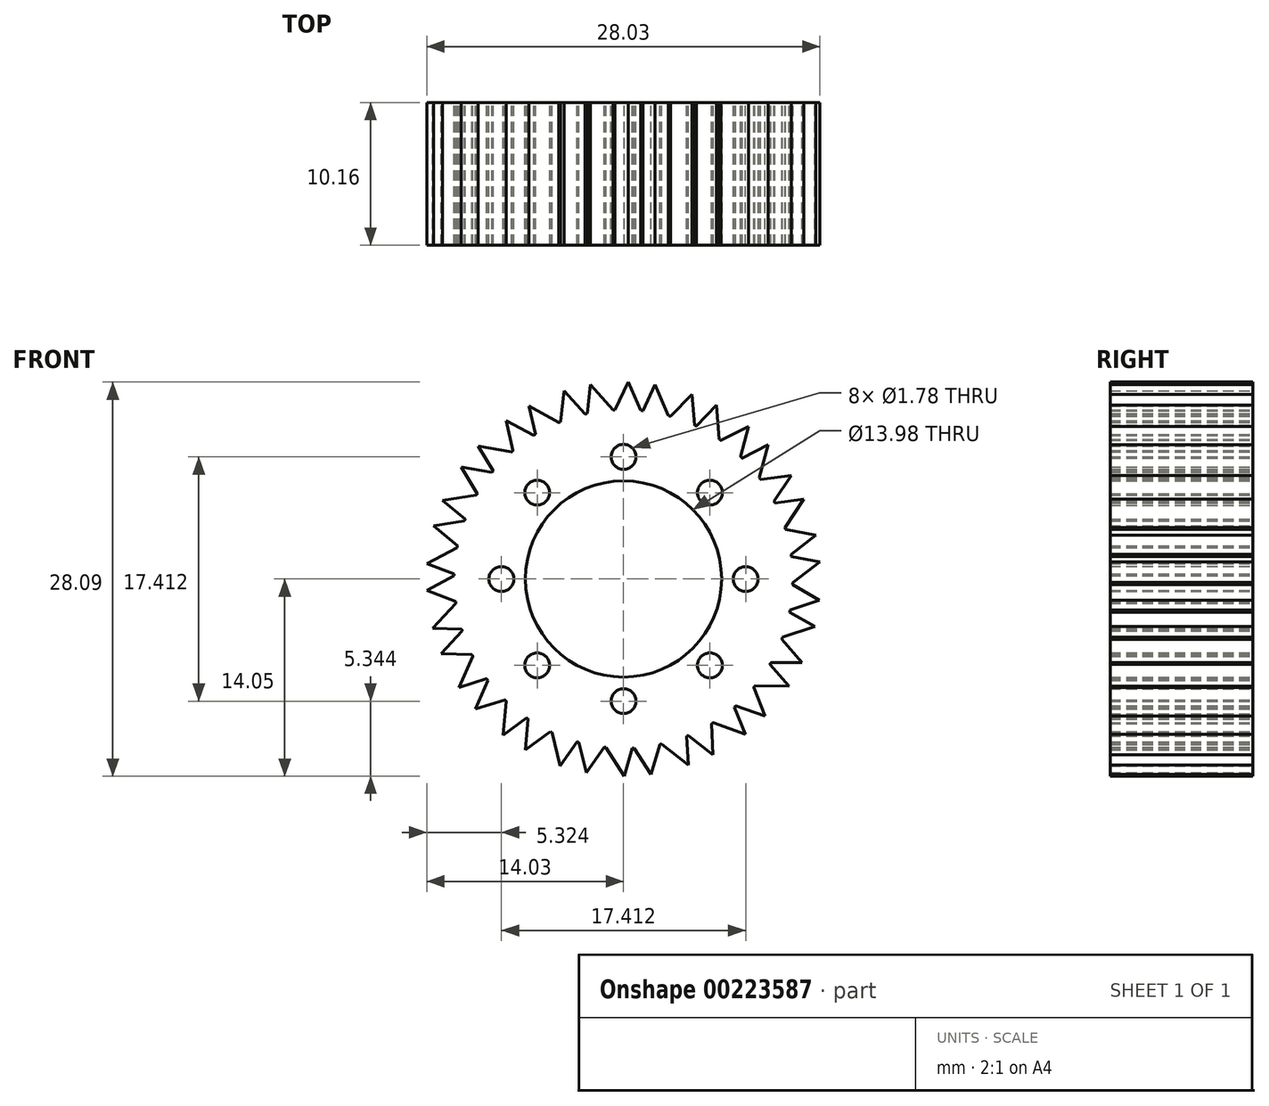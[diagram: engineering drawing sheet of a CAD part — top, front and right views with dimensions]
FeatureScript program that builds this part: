
annotation { "Feature Type Name" : "Feature", "Feature Type Description" : "" }
export const myFeature = defineFeature(function(context is Context, id is Id, definition is map)
    precondition{}
    {
        {
            var Q0;
            Q0=qCreatedBy(makeId("Front.planeOp"),FACE);
            var sketch = newSketch(context, id + "F0", { "sketchPlane" : qUnion([Q0])});
            skCircle(sketch, "E0", {"center": v(0, 0) * mm, "radius": 7 * mm});
            skCircle(sketch, "E1.0", {"center": v(0, 0) * mm, "radius": 12.07 * mm});
            skCircle(sketch, "E2", {"center": v(0, 8.7) * mm, "radius": 0.89 * mm});
            skCircle(sketch, "E3.1.0", {"center": v(-6.16, 6.16) * mm, "radius": 0.89 * mm});
            skCircle(sketch, "E3.2.0", {"center": v(-8.7, 0) * mm, "radius": 0.89 * mm});
            skCircle(sketch, "E3.3.0", {"center": v(-6.16, -6.16) * mm, "radius": 0.89 * mm});
            skCircle(sketch, "E3.4.0", {"center": v(0, -8.7) * mm, "radius": 0.89 * mm});
            skCircle(sketch, "E3.5.0", {"center": v(6.16, -6.16) * mm, "radius": 0.89 * mm});
            skCircle(sketch, "E3.6.0", {"center": v(8.7, 0) * mm, "radius": 0.89 * mm});
            skCircle(sketch, "E3.7.0", {"center": v(6.16, 6.16) * mm, "radius": 0.89 * mm});
            skLineSegment(sketch, "E4", {"start": v(-0.6, 12.06) * mm, "end": v(0.35, 14.04) * mm});
            skLineSegment(sketch, "E5", {"start": v(0.35, 14.04) * mm, "end": v(1.3, 11.85) * mm});
            skLineSegment(sketch, "E6", {"start": v(3.2, 11.64) * mm, "end": v(2.26, 13.87) * mm});
            skLineSegment(sketch, "E7", {"start": v(2.26, 13.87) * mm, "end": v(1.3, 11.85) * mm});
            skLineSegment(sketch, "E8.1.0", {"start": v(-4.49, 11.2) * mm, "end": v(-4.23, 13.4) * mm});
            skLineSegment(sketch, "E8.1.1", {"start": v(-4.23, 13.4) * mm, "end": v(-2.61, 11.63) * mm});
            skLineSegment(sketch, "E8.1.2", {"start": v(-2.37, 13.85) * mm, "end": v(-2.61, 11.63) * mm});
            skLineSegment(sketch, "E8.1.3", {"start": v(-0.74, 12.05) * mm, "end": v(-2.37, 13.85) * mm});
            skLineSegment(sketch, "E8.2.0", {"start": v(-7.88, 9.14) * mm, "end": v(-8.35, 11.3) * mm});
            skLineSegment(sketch, "E8.2.1", {"start": v(-8.35, 11.3) * mm, "end": v(-6.25, 10.15) * mm});
            skLineSegment(sketch, "E8.2.2", {"start": v(-6.74, 12.33) * mm, "end": v(-6.25, 10.15) * mm});
            skLineSegment(sketch, "E8.2.3", {"start": v(-4.61, 11.15) * mm, "end": v(-6.74, 12.33) * mm});
            skLineSegment(sketch, "E8.3.0", {"start": v(-10.42, 6.09) * mm, "end": v(-11.57, 7.97) * mm});
            skLineSegment(sketch, "E8.3.1", {"start": v(-11.57, 7.97) * mm, "end": v(-9.2, 7.57) * mm});
            skLineSegment(sketch, "E8.3.2", {"start": v(-10.38, 9.47) * mm, "end": v(-9.2, 7.57) * mm});
            skLineSegment(sketch, "E8.3.3", {"start": v(-7.99, 9.05) * mm, "end": v(-10.38, 9.47) * mm});
            skLineSegment(sketch, "E8.4.0", {"start": v(-11.84, 2.37) * mm, "end": v(-13.53, 3.79) * mm});
            skLineSegment(sketch, "E8.4.1", {"start": v(-13.53, 3.79) * mm, "end": v(-11.16, 4.17) * mm});
            skLineSegment(sketch, "E8.4.2", {"start": v(-12.9, 5.6) * mm, "end": v(-11.16, 4.17) * mm});
            skLineSegment(sketch, "E8.4.3", {"start": v(-10.5, 5.97) * mm, "end": v(-12.9, 5.6) * mm});
            skLineSegment(sketch, "E8.5.0", {"start": v(-11.97, -1.6) * mm, "end": v(-14.03, -0.81) * mm});
            skLineSegment(sketch, "E8.5.1", {"start": v(-14.03, -0.81) * mm, "end": v(-11.91, 0.32) * mm});
            skLineSegment(sketch, "E8.5.2", {"start": v(-14, 1.1) * mm, "end": v(-11.91, 0.32) * mm});
            skLineSegment(sketch, "E8.5.3", {"start": v(-11.86, 2.24) * mm, "end": v(-14, 1.1) * mm});
            skLineSegment(sketch, "E8.6.0", {"start": v(-10.8, -5.4) * mm, "end": v(-13, -5.32) * mm});
            skLineSegment(sketch, "E8.6.1", {"start": v(-13, -5.32) * mm, "end": v(-11.37, -3.57) * mm});
            skLineSegment(sketch, "E8.6.2", {"start": v(-13.6, -3.5) * mm, "end": v(-11.37, -3.57) * mm});
            skLineSegment(sketch, "E8.6.3", {"start": v(-11.95, -1.74) * mm, "end": v(-13.6, -3.5) * mm});
            skLineSegment(sketch, "E8.7.0", {"start": v(-8.46, -8.6) * mm, "end": v(-10.57, -9.25) * mm});
            skLineSegment(sketch, "E8.7.1", {"start": v(-10.57, -9.25) * mm, "end": v(-9.6, -7.06) * mm});
            skLineSegment(sketch, "E8.7.2", {"start": v(-11.73, -7.73) * mm, "end": v(-9.6, -7.06) * mm});
            skLineSegment(sketch, "E8.7.3", {"start": v(-10.74, -5.52) * mm, "end": v(-11.73, -7.73) * mm});
            skLineSegment(sketch, "E8.8.0", {"start": v(-5.2, -10.9) * mm, "end": v(-7, -12.19) * mm});
            skLineSegment(sketch, "E8.8.1", {"start": v(-7, -12.19) * mm, "end": v(-6.78, -9.8) * mm});
            skLineSegment(sketch, "E8.8.2", {"start": v(-8.58, -11.12) * mm, "end": v(-6.78, -9.8) * mm});
            skLineSegment(sketch, "E8.8.3", {"start": v(-8.36, -8.7) * mm, "end": v(-8.58, -11.12) * mm});
            skLineSegment(sketch, "E8.9.0", {"start": v(-1.39, -12) * mm, "end": v(-2.66, -13.8) * mm});
            skLineSegment(sketch, "E8.9.1", {"start": v(-2.66, -13.8) * mm, "end": v(-3.24, -11.47) * mm});
            skLineSegment(sketch, "E8.9.2", {"start": v(-4.5, -13.3) * mm, "end": v(-3.24, -11.47) * mm});
            skLineSegment(sketch, "E8.9.3", {"start": v(-5.08, -10.95) * mm, "end": v(-4.5, -13.3) * mm});
            skLineSegment(sketch, "E8.10.0", {"start": v(2.58, -11.8) * mm, "end": v(1.97, -13.91) * mm});
            skLineSegment(sketch, "E8.10.1", {"start": v(1.97, -13.91) * mm, "end": v(0.66, -11.9) * mm});
            skLineSegment(sketch, "E8.10.2", {"start": v(0.06, -14.05) * mm, "end": v(0.66, -11.9) * mm});
            skLineSegment(sketch, "E8.10.3", {"start": v(-1.25, -12) * mm, "end": v(0.06, -14.05) * mm});
            skLineSegment(sketch, "E8.11.0", {"start": v(6.27, -10.32) * mm, "end": v(6.38, -12.52) * mm});
            skLineSegment(sketch, "E8.11.1", {"start": v(6.38, -12.52) * mm, "end": v(4.5, -11.04) * mm});
            skLineSegment(sketch, "E8.11.2", {"start": v(4.62, -13.27) * mm, "end": v(4.5, -11.04) * mm});
            skLineSegment(sketch, "E8.11.3", {"start": v(2.72, -11.76) * mm, "end": v(4.62, -13.27) * mm});
            skLineSegment(sketch, "E8.12.0", {"start": v(9.28, -7.72) * mm, "end": v(10.1, -9.77) * mm});
            skLineSegment(sketch, "E8.12.1", {"start": v(10.1, -9.77) * mm, "end": v(7.83, -8.98) * mm});
            skLineSegment(sketch, "E8.12.2", {"start": v(8.68, -11.05) * mm, "end": v(7.83, -8.98) * mm});
            skLineSegment(sketch, "E8.12.3", {"start": v(6.39, -10.24) * mm, "end": v(8.68, -11.05) * mm});
            skLineSegment(sketch, "E8.13.0", {"start": v(11.28, -4.3) * mm, "end": v(12.72, -5.96) * mm});
            skLineSegment(sketch, "E8.13.1", {"start": v(12.72, -5.96) * mm, "end": v(10.33, -5.95) * mm});
            skLineSegment(sketch, "E8.13.2", {"start": v(11.8, -7.64) * mm, "end": v(10.33, -5.95) * mm});
            skLineSegment(sketch, "E8.13.3", {"start": v(9.37, -7.61) * mm, "end": v(11.8, -7.64) * mm});
            skLineSegment(sketch, "E8.14.0", {"start": v(12.06, -0.4) * mm, "end": v(13.97, -1.5) * mm});
            skLineSegment(sketch, "E8.14.1", {"start": v(13.97, -1.5) * mm, "end": v(11.7, -2.28) * mm});
            skLineSegment(sketch, "E8.14.2", {"start": v(13.63, -3.4) * mm, "end": v(11.7, -2.28) * mm});
            skLineSegment(sketch, "E8.14.3", {"start": v(11.33, -4.16) * mm, "end": v(13.63, -3.4) * mm});
            skLineSegment(sketch, "E8.15.0", {"start": v(11.54, 3.54) * mm, "end": v(13.7, 3.1) * mm});
            skLineSegment(sketch, "E8.15.1", {"start": v(13.7, 3.1) * mm, "end": v(11.8, 1.65) * mm});
            skLineSegment(sketch, "E8.15.2", {"start": v(14, 1.22) * mm, "end": v(11.8, 1.65) * mm});
            skLineSegment(sketch, "E8.15.3", {"start": v(12.07, -0.25) * mm, "end": v(14, 1.22) * mm});
            skLineSegment(sketch, "E8.16.0", {"start": v(9.76, 7.1) * mm, "end": v(11.95, 7.39) * mm});
            skLineSegment(sketch, "E8.16.1", {"start": v(11.95, 7.39) * mm, "end": v(10.63, 5.39) * mm});
            skLineSegment(sketch, "E8.16.2", {"start": v(12.84, 5.7) * mm, "end": v(10.63, 5.39) * mm});
            skLineSegment(sketch, "E8.16.3", {"start": v(11.5, 3.68) * mm, "end": v(12.84, 5.7) * mm});
            skLineSegment(sketch, "E8.17.0", {"start": v(6.93, 9.88) * mm, "end": v(8.9, 10.87) * mm});
            skLineSegment(sketch, "E8.17.1", {"start": v(8.9, 10.87) * mm, "end": v(8.3, 8.55) * mm});
            skLineSegment(sketch, "E8.17.2", {"start": v(10.3, 9.56) * mm, "end": v(8.3, 8.55) * mm});
            skLineSegment(sketch, "E8.17.3", {"start": v(9.68, 7.21) * mm, "end": v(10.3, 9.56) * mm});
            skLineSegment(sketch, "E8.18.0", {"start": v(3.34, 11.6) * mm, "end": v(4.9, 13.17) * mm});
            skLineSegment(sketch, "E8.18.1", {"start": v(4.9, 13.17) * mm, "end": v(5.08, 10.78) * mm});
            skLineSegment(sketch, "E8.18.2", {"start": v(6.64, 12.38) * mm, "end": v(5.08, 10.78) * mm});
            skLineSegment(sketch, "E8.18.3", {"start": v(6.81, 9.96) * mm, "end": v(6.64, 12.38) * mm});
            skSolve(sketch);
        }
        {
            var Q0;
            Q0 = qSketchRegion(id + "F0", true);
            extrude(context, id + "F1", {"entities" : qUnion([Q0]), "depth" : 10.16 * mm});
        }
    });
